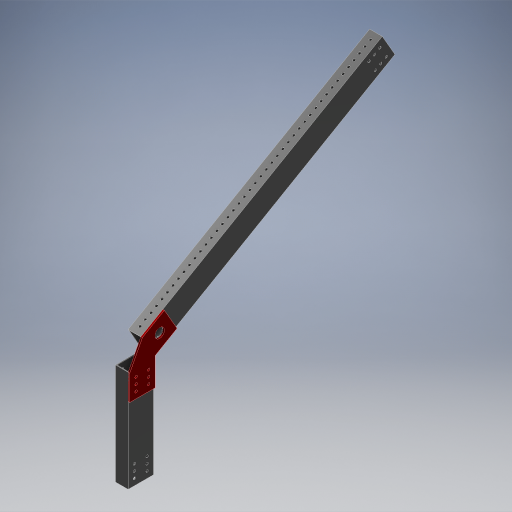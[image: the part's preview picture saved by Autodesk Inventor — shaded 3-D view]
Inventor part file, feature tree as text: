
AUTODESK INVENTOR PART (.ipt)
format: ipt  version: 2024.2 (Build 282272000, 272)  size: 643,584 bytes
history: native  units: in
note: dims shown in document units (in); Inventor stores cm internally (conversion verified against a paired STEP export)
features: extrude x6, sketch x5, projected_geometry x5, other x3
ambient origin geometry x8: Origin, YZ Plane, XZ Plane, XY Plane, X Axis, Y Axis, Z Axis, Center Point
bodies: Body1 (feature_tree), Body2 (feature_tree), Body3 (feature_tree)
feature tree (19):
  other  "2024-210-001-Backright-Support"
  sketch  "Sketch1"  dims[d0=1.0in d1=28.0in]
  extrude  "Extrusion1"  Depth=1.0in
  extrude  "Extrusion2"  Depth=0.196in
  extrude  "Extrusion5"  Depth=0.5in
  extrude  "Extrusion6"  Depth=0.196in
  extrude  "Extrusion7"  Depth=0.125in
  extrude  "Extrusion8"  Depth=0.3937in
  other  "2024-210-002-Angle-Beam"
  sketch  "Sketch3"  dims[d3=26.0in d4=0.196in]
  projected_geometry  "Projected Loop3"
  sketch  "Sketch4"  dims[d5=0.5in d6=0.5in]
  projected_geometry  "Projected Loop4"
  sketch  "Sketch5"  dims[d7=1.1811in d9=0.5in d10=19.2913in d12=0.5in d15=0.196in]
  projected_geometry  "Projected Loop5"
  sketch  "Sketch6"  dims[d16=0.5in d17=0.5in d18=20.8661in d20=0.5in d21=0.3937in d23=1.0in d25=8.0in d26=2.0in d28=2.0in d29=2.0in d31=4.0in d34=0.2in d37=22.0in d38=11.0in d39=0.196in d40=0.5in d41=0.5in d42=0.7874in d44=1.0in d45=1.1811in d47=0.5in d50=0.75in d51=0.196in d52=0.5in d53=0.5in d54=0.7874in d56=1.0in d57=1.1811in d59=0.5in d62=0.196in d63=0.5in d64=0.5in d65=0.7874in d67=1.0in d68=1.1811in d70=0.5in d73=1.0in d74=0.0in d75=1.0in d76=0.0in d79=30.0deg d80=1.0in d81=1.0in d86=0.0625in d87=21.875in d88=0.0in d89=0.0625in d90=0.0in d91=0.0in d92=0.196in d93=0.5in d94=0.5in d95=16.9291in d97=0.5in d98=0.3937in d100=1.0in d102=2.0in d103=0.0in d105=9.0in d106=1.0in d107=-0.1718in d108=2.0in d109=2.0in d110=0.125in d111=0.0in]
  projected_geometry  "Projected Loop6"
  projected_geometry  "Projected Loop7"
  other  "2024-210-003-Dead-Axle-Gusset"
